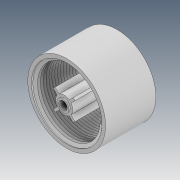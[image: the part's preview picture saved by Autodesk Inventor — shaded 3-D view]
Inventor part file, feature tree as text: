
AUTODESK INVENTOR PART (.ipt)
format: ipt  version: 2020 (Build 240168000, 168)  size: 468,480 bytes
history: native  units: mm
features: sketch x5, extrude x4, plane x1, helix x1, chamfer x1
ambient origin geometry x8: Origin, YZ Plane, XZ Plane, XY Plane, X Axis, Y Axis, Z Axis, Center Point
bodies: Solid1 (feature_tree)
feature tree (12):
  extrude  "Extrusion1"  Depth=1.6mm
  extrude  "Extrusion2"  Depth=8.0mm
  extrude  "Extrusion3"  Depth=40.0mm TaperAngle=360.0deg
  sketch  "Sketch4"  dims[d11=3.7mm d12=2.0mm d13=0.0mm d14=7.5mm]
  plane  "Work Plane1"
  extrude  "Extrusion4"  Depth=2.0mm TaperAngle=0.0deg
  helix  "Coil3"  [1 undecoded]
  chamfer  "Chamfer1"  Angle=45.0deg  [1 undecoded]
  sketch  "Sketch1"  dims[d1=30.8mm d2=1.6mm]
  sketch  "Sketch2"  dims[d3=20.0mm d4=0.0mm d5=8.0mm]
  sketch  "Sketch3"  dims[d6=8.0mm d7=40.0mm d9=360.0deg]
  sketch  "Sketch6"  dims[d15=1.11mm d16=45.0deg d17=1.11mm d18=45.0deg d19=12.33mm d20=12.33mm d21=21.11mm d22=0.0mm d45=-0.9mm d51=5.3mm d52=0.5mm d53=0.0mm d54=1.4mm d55=1.25mm d56=1.25mm d57=20.0mm d58=10.0mm d59=0.0mm d60=90.0deg d61=90.0deg d62=0.0mm d63=0.0mm d64=0.559mm d65=2.0mm d66=45.0deg]
note: 2 required parameter values undecoded (feature->parameter linkage not recoverable at this tier; creation-order binding heuristic only, values carry confidence <= 0.55)
